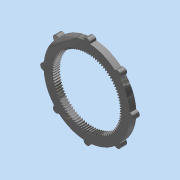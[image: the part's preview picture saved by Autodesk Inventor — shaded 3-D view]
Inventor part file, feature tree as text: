
AUTODESK INVENTOR PART (.ipt)
format: ipt  version: 2015 (Build 190159000, 159)  size: 507,392 bytes
history: native  units: in
note: dims shown in document units (in); Inventor stores cm internally (conversion verified against a paired STEP export)
features: pattern_circular x2, extrude x2, sketch x2, other x1, direct_edit x1, imported_body x1, move_body x1
ambient origin geometry x8: Origin, YZ Plane, XZ Plane, XY Plane, X Axis, Y Axis, Z Axis, Center Point
bodies: Solid1 (feature_tree)
feature tree (10):
  other  "a_1b10-n480961"
  direct_edit  "Direct Edit1"
  pattern_circular  "Circular Pattern1"  Count=48 Angle=360.0deg
  extrude  "Extrusion1"  TaperAngle=0.0deg  [1 undecoded]
  extrude  "Extrusion2"  Depth=1.0in
  pattern_circular  "Circular Pattern2"  [2 undecoded]
  imported_body  "Base1"
  sketch  "Sketch1"  dims[d0=0.0in d1=0.0in d2=0.0625in d3=18.8976in d4=360.0deg]
  sketch  "Sketch2"  dims[d6=2.5591in d7=0.0in d8=0.0in d9=0.1969in d10=1.0in d11=0.0in d12=3.1496in d13=360.0deg]
  move_body  "Move1"
note: 3 required parameter values undecoded (feature->parameter linkage not recoverable at this tier; creation-order binding heuristic only, values carry confidence <= 0.55)
